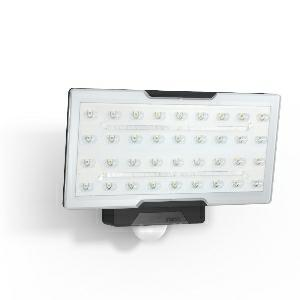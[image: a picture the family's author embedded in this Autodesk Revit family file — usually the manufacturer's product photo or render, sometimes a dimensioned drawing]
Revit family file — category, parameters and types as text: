
# Revit family: xled_pro_wide_010096
name_source: partatom
category: Leuchten
revit_build: Autodesk Revit 2016 (Build: 20190508_0715(x64)
units: mm (PartAtom-declared; Revit-internal decimal feet)

## family parameters
Basisbauteil = Fläche
Beim Laden mit Abzugskörper schneiden = Nein
Bemaßung runder Anschluss = Durchmesser verwenden
Gemeinsam genutzt = Nein
Lichtquelle = Nein
Raumberechnungspunkt = Nein
Teiletyp = Normal

## types (1)
- XLED PRO Wide (1 x , 2400 lm, 4000 K)
    Beschreibung = Dimensions (L x W x H): 126 x 265 x 188 mm; Mains power supply: 220 – 240 V / 50 – 60 Hz; Mounting height max.: 6,00 m; Sensor Technology: passive infrared; Output: 24,8 W; Interconnection: Yes; Type of interconnection: Sensor/slave; Interconnection, number: maximum of 10 floodlights; Luminous flux: 2400 lm; Colour temperature: 4000 K; Colour variation LED: SDCM3; Colour Rendering Index CRI: 80-89; With lamp: Yes, STEINEL LED system; Lamp: LED cannot be replaced; LED life expectancy (max. °C): 50000 h; Drop in luminous flux in accordance with LM80: L70B10; LED cooling system: Passive Thermo Control; With motion detector: Yes; Detection angle: 240 °; Angle of aperture: 180 °; Sneak-by guard: Yes; Capability of masking out individual segments: Yes; Reach, radial: r = 3 m (19 m²); Reach, tangential: r = 12 m (302 m²); Photo-cell controller: Yes; Twilight setting: 2 – 1000 lx; Time setting: 5 sec – 15 min; Basic light level function: Yes; Basic light level function time: 10 min, 30 min, all night; Soft light start: No; Continuous light: selectable, 4h; Impact resistance: IK03; IP-rating: IP54; Protection class: I; Ambient temperature: -20 – 40 °C; Housing material: Aluminium; Cover material: Plastic, transparent; Manufacturer's Warranty: 5 years; PU1, net weight: 1,841 kg; Version: black; PU1, EAN: 4007841010096
    CIE Flux Codes = 47 82 96 99 102
    Color Rendering = 80-89
    Color Temperature = 4000 K
    Frequency = 50 Hz, 60 Hz
    Height = 188 mm  [stored 0.616798 ft]
    Hersteller = Steinel
    Lamp Light Flux = 2400 lm
    Lamp count = 1
    Lampe = 1 x
    Length = 126 mm
    Luminous efficacy = 100 lm/W
    ModVariant = Nein
    Modell = 010096
    Mounting Type = Surface mounted
    Number of Poles = 1
    OnlyDefault = Ja
    Power Factor = 1
    Product Name = XLED PRO Wide
    Product group = Sensor-switched indoor light
    ProductGroupID = 30
    Protection Class = Protection class I
    Protection Degree = IP 54
    RlxData = <blob elided: 124233 chars, md5=1ccd9879>
    Scheinlast = 24 VA
    Socket = socket
    Standby Power = 0 W
    System Light Flux = 2400 lm
    System Power = 24 W
    Typenbild = produkt1_010096.jpg
    Typenkommentare = Product without accessories
    URL = http://relux.com
    VarID = ---
    Voltage = 0 V
    Vorgabe-Ansicht = 1800 mm
    Weight = 0.00 kg
    Width = 265 mm

note: [stored X ft] marks values corroborated as IEEE doubles in the binary element streams (Revit-internal decimal feet)

## geometry (parser evidence)
native form markers: Blend x4, Sweep x14
no freeform markers — native parametric forms only
